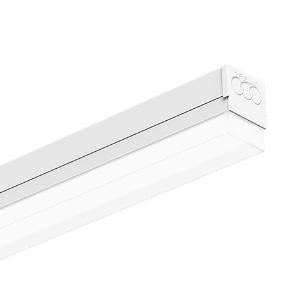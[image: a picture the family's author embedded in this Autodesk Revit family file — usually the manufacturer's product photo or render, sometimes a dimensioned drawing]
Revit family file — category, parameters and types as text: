
# Revit family: 3f_filippi_-_3f_zeta_dr_3f_filippi_-_10879_-_3f_zeta_dr_1x9_led_l605
name_source: partatom
category: Lighting Fixtures
units: mm (PartAtom-declared; Revit-internal decimal feet)

## family parameters
Cut with Voids When Loaded = No
Host = Face
Light Source = No
Part Type = Normal
Room Calculation Point = No
Round Connector Dimension = Use Diameter
Shared = No

## types (1)
- 3F Filippi - 3F Zeta DR (1 x LED, 1212 lm, 10 W, 4000 K)
    Apparent Load = 10 VA
    Approval mark = CE
    CIE Flux Codes = 41 72 91 86 100
    Color Rendering = 80
    Color Temperature = 4000 K
    Control Gear = Electronic ballast
    Default Elevation = 1800 mm
    Description = ILLUMINOTECHNICAL
Luminous efficiency 100% (DLOR 86%, ULOR 14%).
Initial luminous flux of the luminaire 1212 lm.
Diffused symmetric distribution.
Installation Interdistance Transv.D = 1.31 x hu - Long.D = 1.25 x hu.
Tabular UGR (CIE 117 - 4H-8H; S=0.25H; 70/50/20): RUG 23.1 - 21.5.
Beam angle: 136° - 112°.
Luminous efficacy 121 lm/W.
Lifetime (L93/B10): 30000 h. (tq+25°C)
Lifetime (L90/B10): 50000 h. (tq+25°C)
Sudden decreased luminous flux after 50000 hours: 0% (C0).
Photobiological safety in compliance with IEC/TR 62778: RG0 risk exempt, (IEC 62471).
In compliance with IEC/EN 62722-2-1 - IEC/EN 62717 standards.

SOURCE
Linear LED module 9W/840.
Energy efficiency class (UE 2019/2020 - UE 2019/2015): D.
CIE 13.3 Colour rendering index: CRI >80 (R9 <50%).
IES TM-30 Fidelity Index: Rf = 84 Rg = 95.
CCT nominal colour temperature 4000 K.
Colour initial tolerance (MacAdam): SDCM 3.

MECHANICAL
Housing in hot-galvanised steel, painted in white polyester, obtained through rolling process.
Light unit in hot-galvanised steel, painted in white polyester base with fixing springs and retractable safety hooks in stainless steel.
Rectangular screen in self-extinguishing polycarbonate, UV stabilised, opal, with smooth outer surface.
End caps in white polycarbonate.
Pair of stainless steel sliding brackets with sliding block screws.
Luminaire with limited surface temperature. - D - (EN 60598-2-24)
Dimensions: 605x62 mm, height 81 mm. Weight 1.53 kg.
IP40 protection degree.
Mechanical strength to impacts IK06 (1 joule).
Glow-wire test resistance 850°C.

ELECTRICAL
Halogen Free electronic wiring 230V-50/60Hz, power factor 0.90, THD <25%, constant output current, SELV, class I, 1 driver.
Power of the luminaire 10 W.
ENEC - CE.
SAFE FLICKER: PstLM=<1 and SVM=<0.4 (IEC TR 61547-1 and IEC TR 63158), to ensure a more comfortable and safe light.
Luminaire compliant with EN 60598-2-22 for power supply from a centralised emergency system CPSS (Central Power Supply System), not incorporated in the luminaire - high risk areas excluded. The default power and flux are 100% in AC and 100% in DC.
Ambient temperature from 0°C to +25°C.
Temperature class T6 max 85°C.
Relative humidity UR: <85%.

INSTALLATION
Ceiling / Suspended / Wall.
All accessories dedicated to this product are available on the Catalog and on our website www.3F-Filippi.com.

APPLICATIONS
Suitable product for food production plants (HACCP), IFS (Food Version 6), BRC (GSFS Food Version 7).
In commercial environments, exhibition areas, shops and stores.

WARNING
Luminaire designed for disposal/recycling at end-of-life.
Replaceable (LED only) light source by a professional. Replaceable control gear by a professional.
    Height = 81 mm
    Lamp = 1 x LED
    Lamp Light Flux = 1212 lm
    Lamp Power = 10 W
    Lamp count = 1
    Length = 605 mm
    Lifetime = 50000 h
    Luminous efficacy = 121 lm/W
    Manufacturer = 3F Filippi
    ModVariant = No
    Model = 3F Filippi - 10879 - 3F Zeta DR 1x9 LED L605
    Mounting Place = Ceiling
    Mounting Type = Pendant
    Number of Poles = 1
    OnlyDefault = Yes
    Power Factor = 1
    Product Name = 3F Filippi - 3F Zeta DR
    Product group = pendant luminaire
    ProductGroupID = 9
    Protection Class = Protection class I
    Protection Degree = IP 40
    RLX_Detail_Level = 1
    RLX_Emergency_Light_Flux = 0 lm
    RLX_Emergency_Type = 0
    RLX_Emergency_Type_DB = No
    RlxData = <blob elided: 32897 chars, md5=66250282>
    Socket = socket
    Standby Power = 0 W
    System Light Flux = 1212 lm
    System Power = 10 W
    Type Comments = Product without accessories
    Type Image = 3ffilippi_3f_zeta_dr.jpg
    URL = http://relux.com
    VarID = ---
    Voltage = 0 V
    Weight = 0.00 kg
    Width = 62 mm  [stored 0.203412 ft]

note: [stored X ft] marks values corroborated as IEEE doubles in the binary element streams (Revit-internal decimal feet)

## geometry (parser evidence)
native form markers: Blend x4, Sweep x14
no freeform markers — native parametric forms only
